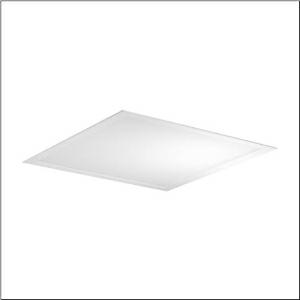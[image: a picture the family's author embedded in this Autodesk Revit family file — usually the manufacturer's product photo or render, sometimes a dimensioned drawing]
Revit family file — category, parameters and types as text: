
# Revit family: apollon_21_square_51mq11wd2114
name_source: partatom
category: Lighting Fixtures
units: mm (PartAtom-declared; Revit-internal decimal feet)

## family parameters
Cut with Voids When Loaded = No
Host = Face
Light Source = No
Part Type = Normal
Room Calculation Point = No
Round Connector Dimension = Use Diameter
Shared = No

## types (1)
- Apollon 21 square (1 x LED, 4100 lm, 24.7 W, 4000K)
    Apparent Load = 25 VA
    CIE Flux Codes = 60 87 97 100 100
    Color Rendering = 90
    Color Temperature = 4000K
    Default Elevation = 1800 mm
    Description = Apollon 21 square, office luminaire, primary optical cover: micro prismatic cover, of PMMA, CAT 2 (L<= 3000cd/m²), light emission: direct distribution, primary light characteristic: symmetric, installation type: lay-in mounting, LED, rated luminous flux: 4.100lm, luminous efficacy: 166lm/W, light colour: 940, colour temperature: 4000K, control gear: DALI 2, Multilumen, with terminal, 5-pole, mains connection: 220..240V, AC/DC, 0/50..60Hz, rated input power: 24.7W, housing, of aluminium, coated, traffic white (RAL 9016), module: M625, length: 620mm, width: 620mm, height: 55mm, recess depth: 180mm, housing upper side, of sheet steel, galvanised, protection rating (complete): IP20, protection rating (lamp compartment, on room side): IP50, insulation class (complete): insulation class II (safety insulation), certification: CE, ENEC, impact resistance: IK03, permissible operating ambient temperature: -20..+45°C, permissible storage temperature: -40..+80°C, standard: EN 60598-2-22, packaging unit: 1 piece
    Height = 0 mm  [stored 0 ft]
    Lamp = 1 x LED
    Lamp Light Flux = 4100 lm
    Lamp Power = 24.7 W
    Lamp count = 1
    Length = 620 mm
    Luminous efficacy = 166 lm/W
    Manufacturer = Siteco
    ModVariant = No
    Model = 51MQ11WD2114
    Mounting Place = Ceiling
    Mounting Type = Recessed
    Number of Poles = 1
    OnlyDefault = Yes
    Power Factor = 1
    Product Name = Apollon 21 square
    Product group = office luminaire | ceiling recessed
    ProductGroupID = 401
    Protection Class = Protection class II
    Protection Degree = IP 20
    RLX_Detail_Level = 1
    RLX_Emergency_Light_Flux = 0 lm
    RLX_Emergency_Type = 0
    RLX_Emergency_Type_DB = No
    RlxData = <blob elided: 13017 chars, md5=c4504311>
    Socket = socket
    Standby Power = 0 W
    System Light Flux = 4100 lm
    System Power = 25 W
    Type Comments = Product without accessories
    Type Image = l_1291054.jpg
    URL = http://relux.com
    VarID = ---
    Voltage = 0 V
    Weight = 0.00 kg
    Width = 620 mm

note: [stored X ft] marks values corroborated as IEEE doubles in the binary element streams (Revit-internal decimal feet)

## geometry (parser evidence)
native form markers: Sweep x10
no freeform markers — native parametric forms only
